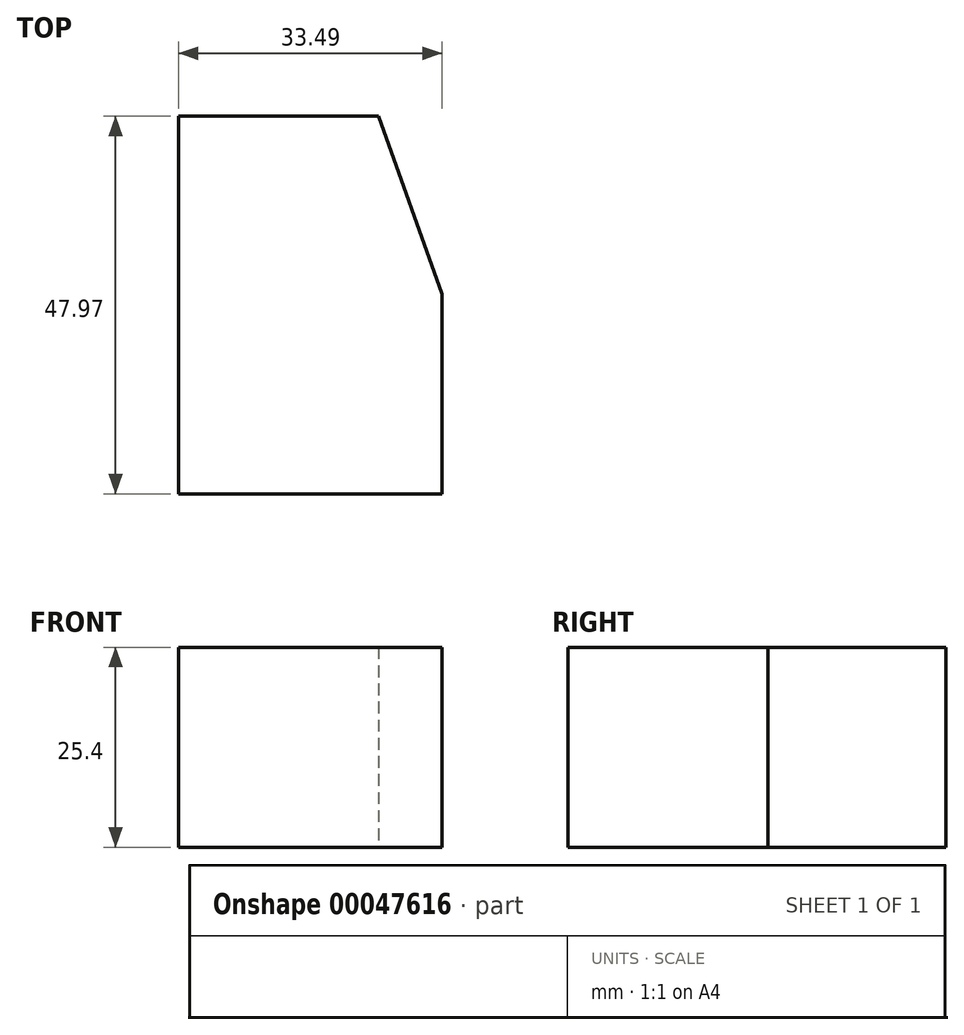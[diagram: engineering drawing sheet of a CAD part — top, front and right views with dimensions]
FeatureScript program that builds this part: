
annotation { "Feature Type Name" : "Feature", "Feature Type Description" : "" }
export const myFeature = defineFeature(function(context is Context, id is Id, definition is map)
    precondition{}
    {
        {
            var Q0;
            Q0=qCreatedBy(makeId("Top.planeOp"),FACE);
            var sketch = newSketch(context, id + "F0", { "sketchPlane" : qUnion([Q0])});
            skLineSegment(sketch, "E0", {"start": v(-85.8, 25) * mm, "end": v(-85.8, 2.43) * mm});
            skLineSegment(sketch, "E1", {"start": v(-85.8, 2.43) * mm, "end": v(-77.72, 2.43) * mm});
            skLineSegment(sketch, "E2", {"start": v(-77.72, 2.43) * mm, "end": v(-85.8, 25) * mm});
            skSolve(sketch);
        }
        {
            var Q0;
            Q0 = qSketchRegion(id + "F0", true);
            extrude(context, id + "F1", {"entities" : qUnion([Q0]), "depth" : 25.4 * mm});
        }
        {
            var Q0;
            Q0=makeQuery(id+"F1.opExtrude","SWEPT_FACE",FACE,{"disambiguationData":[OSD([sQuery(id+"F0.wireOp",EDGE,"E0")])]});
            extrude(context, id + "F2", {"entities" : qUnion([Q0]), "operationType" : NewBodyOperationType.ADD, "depth" : 25.4 * mm});
        }
        {
            var Q0;
            {var subQ0=sQuery(id+"F0.wireOp",EDGE,"E1");Q0=makeQuery(id+"F2.boolean.opBoolean","MERGE",FACE,{"derivedFrom":[makeQuery(id+"F1.opExtrude","SWEPT_FACE",FACE,{"disambiguationData":[OSD([subQ0])]}),makeQuery(id+"F2.opExtrude","SWEPT_FACE",FACE,{"disambiguationData":[OSD([sQuery(id+"F0.wireOp",EDGE,"E0"),subQ0])]})]});}
            extrude(context, id + "F3", {"entities" : qUnion([Q0]), "operationType" : NewBodyOperationType.ADD, "depth" : 25.4 * mm});
        }
    });
